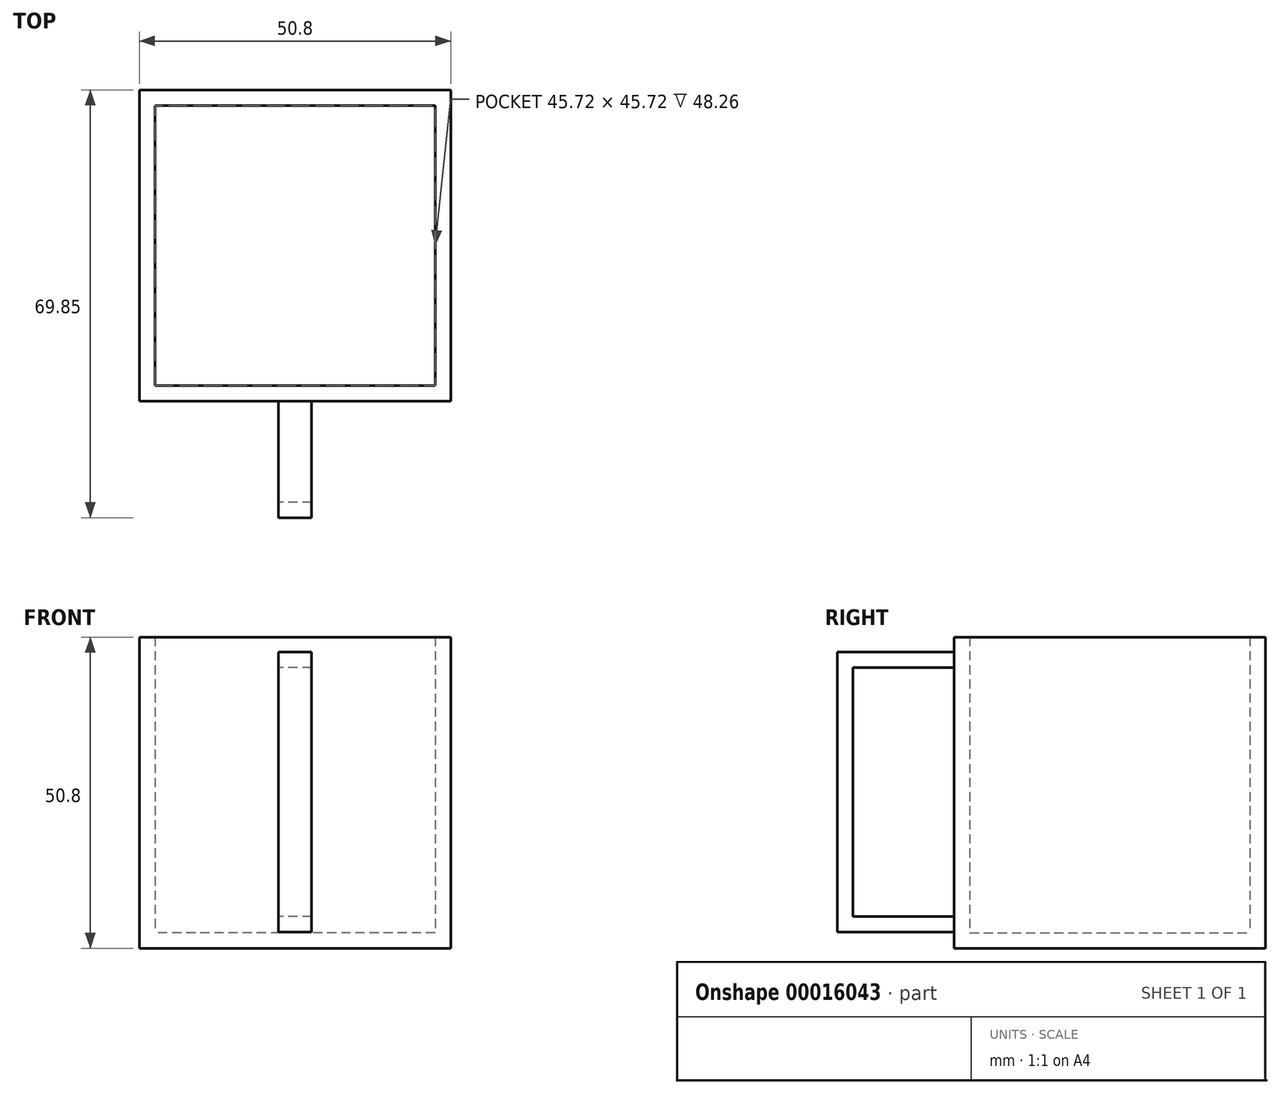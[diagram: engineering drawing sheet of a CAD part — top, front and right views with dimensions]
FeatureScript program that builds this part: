
annotation { "Feature Type Name" : "Feature", "Feature Type Description" : "" }
export const myFeature = defineFeature(function(context is Context, id is Id, definition is map)
    precondition{}
    {
        {
            var Q0;
            Q0=qCreatedBy(makeId("Top.planeOp"),FACE);
            var sketch = newSketch(context, id + "F0", { "sketchPlane" : qUnion([Q0])});
            skLineSegment(sketch, "E0.rect.bottom", {"start": v(25.4, -25.4) * mm, "end": v(-25.4, -25.4) * mm});
            skLineSegment(sketch, "E0.rect.top", {"start": v(25.4, 25.4) * mm, "end": v(-25.4, 25.4) * mm});
            skLineSegment(sketch, "E0.rect.left", {"start": v(25.4, -25.4) * mm, "end": v(25.4, 25.4) * mm});
            skLineSegment(sketch, "E0.rect.right", {"start": v(-25.4, -25.4) * mm, "end": v(-25.4, 25.4) * mm});
            skPoint(sketch, "E0.rect.middle", {"position": v(0, 0) * mm});
            skSolve(sketch);
        }
        {
            var Q0;
            Q0=makeQuery(id+"F0.imprint","IMPRINT",FACE,{"disambiguationData":[TD([[makeQuery(id+"F0.imprint","IMPRINT",EDGE,{"derivedFrom":sQuery(id+"F0.wireOp",EDGE,"E0.rect.bottom")}),-1.0]])]});
            extrude(context, id + "F1", {"entities" : qUnion([Q0]), "depth" : 50.8 * mm});
        }
        {
            var Q0;
            Q0=makeQuery(id+"F1.opExtrude","CAP_FACE",FACE,{"disambiguationData":[OSD([sQuery(id+"F0.wireOp",EDGE,"E0.rect.bottom"),sQuery(id+"F0.wireOp",EDGE,"E0.rect.top"),sQuery(id+"F0.wireOp",EDGE,"E0.rect.left"),sQuery(id+"F0.wireOp",EDGE,"E0.rect.right")])],"isStart":false});
            shell(context, id + "F2", {"entities" : qUnion([Q0]), "thickness" : 2.54 * mm});
        }
        {
            var Q0;
            Q0=makeQuery(id+"F1.opExtrude","SWEPT_FACE",FACE,{"disambiguationData":[OSD([sQuery(id+"F0.wireOp",EDGE,"E0.rect.bottom")])]});
            var sketch = newSketch(context, id + "F3", { "sketchPlane" : qUnion([Q0])});
            skLineSegment(sketch, "E1.rect.bottom", {"start": v(2.71, 2.64) * mm, "end": v(-2.71, 2.64) * mm});
            skLineSegment(sketch, "E1.rect.top", {"start": v(2.71, 48.38) * mm, "end": v(-2.71, 48.38) * mm});
            skLineSegment(sketch, "E1.rect.left", {"start": v(2.71, 2.64) * mm, "end": v(2.71, 48.38) * mm});
            skLineSegment(sketch, "E1.rect.right", {"start": v(-2.71, 2.64) * mm, "end": v(-2.71, 48.38) * mm});
            skPoint(sketch, "E1.rect.middle", {"position": v(0, 25.51) * mm});
            skSolve(sketch);
        }
        {
            var Q0;
            Q0=makeQuery(id+"F3.imprint","IMPRINT",FACE,{"disambiguationData":[TD([[makeQuery(id+"F3.imprint","IMPRINT",EDGE,{"derivedFrom":sQuery(id+"F3.wireOp",EDGE,"E1.rect.bottom")}),-1.0]])]});
            extrude(context, id + "F4", {"entities" : qUnion([Q0]), "operationType" : NewBodyOperationType.ADD, "depth" : 19.05 * mm});
        }
        {
            var Q0;
            Q0=makeQuery(id+"F4.opExtrude","SWEPT_FACE",FACE,{"disambiguationData":[OSD([sQuery(id+"F3.wireOp",EDGE,"E1.rect.right")])]});
            var Q1;
            Q1=makeQuery(id+"F4.opExtrude","SWEPT_FACE",FACE,{"disambiguationData":[OSD([sQuery(id+"F3.wireOp",EDGE,"E1.rect.left")])]});
            shell(context, id + "F5", {"entities" : qUnion([Q0, Q1]), "thickness" : 2.54 * mm});
        }
    });
